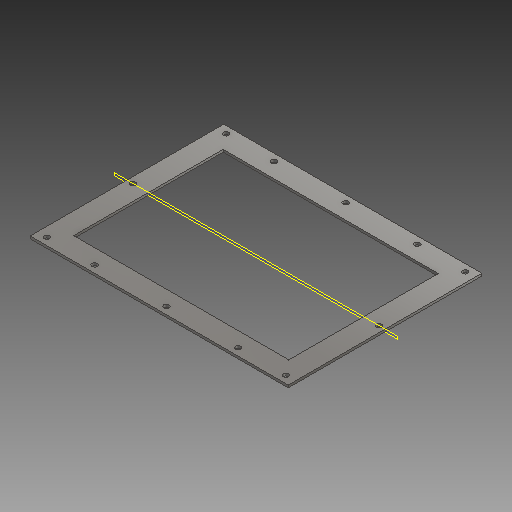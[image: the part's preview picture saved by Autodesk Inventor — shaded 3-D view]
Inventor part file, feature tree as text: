
AUTODESK INVENTOR PART (.ipt)
format: ipt  version: 2018 (Build 220112000, 112)  size: 166,912 bytes
history: native  units: mm
features: other x4, sketch x1
ambient origin geometry x8: Origin, YZ Plane, XZ Plane, XY Plane, X Axis, Y Axis, Z Axis, Center Point
bodies: Body1 (feature_tree)
feature tree (5):
  other  "Fläche2"
  other  "Mittelebene"
  sketch  "Skizze1"  dims[d1=180.0mm d2=125.0mm d3=162.0mm d4=216.0mm d5=2.0mm]
  other  "Grobblech2"
  other  "Definition1"
